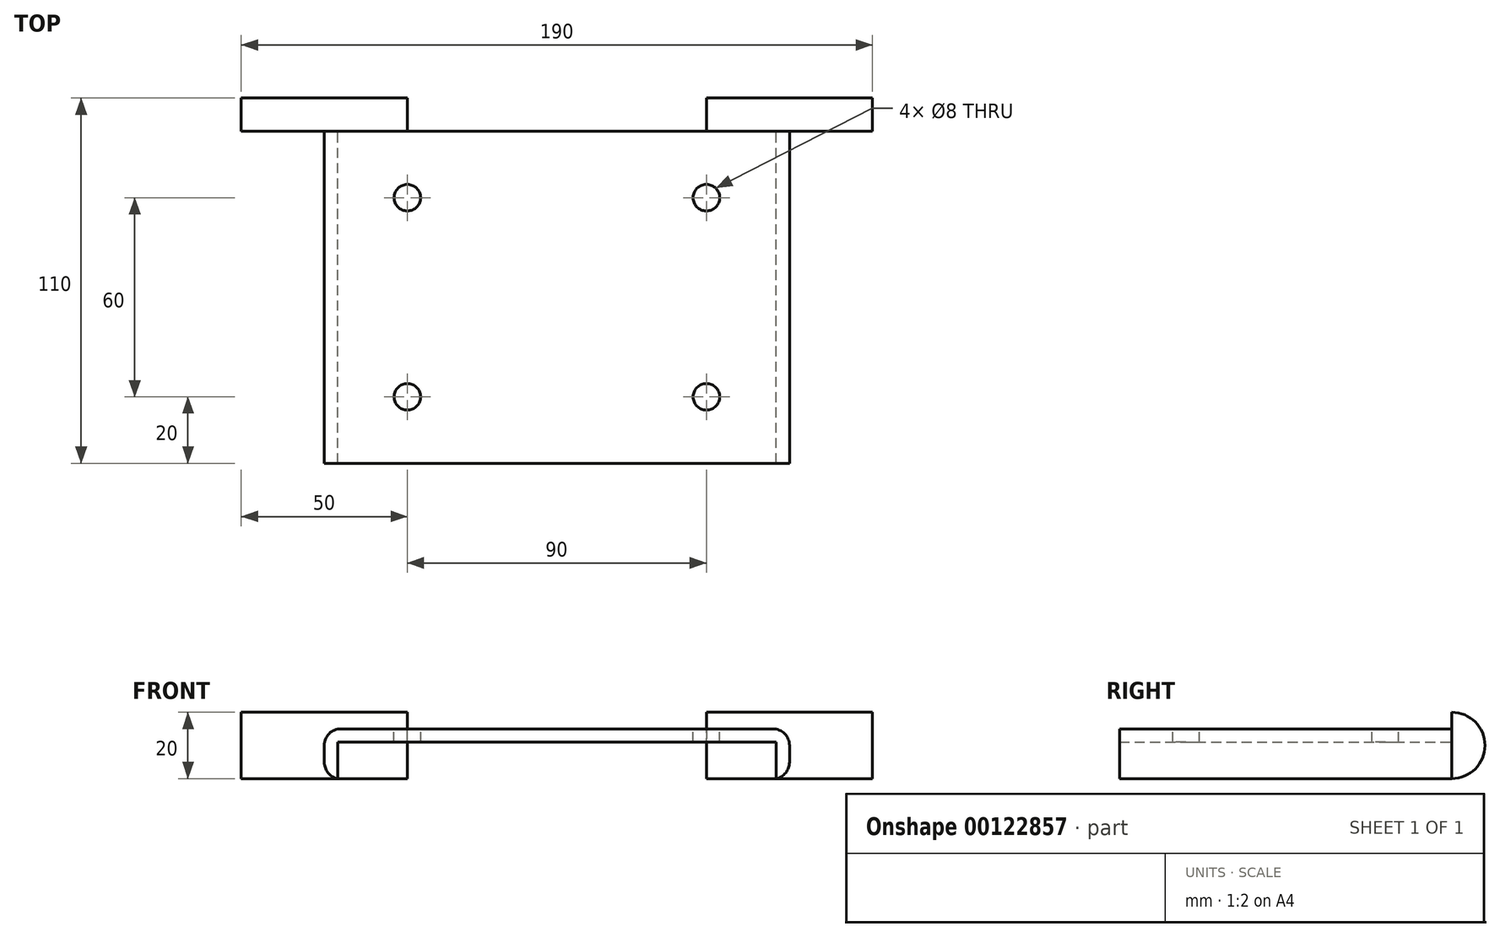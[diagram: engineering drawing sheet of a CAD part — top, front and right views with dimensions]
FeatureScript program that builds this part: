
annotation { "Feature Type Name" : "Feature", "Feature Type Description" : "" }
export const myFeature = defineFeature(function(context is Context, id is Id, definition is map)
    precondition{}
    {
        {
            var Q0;
            Q0=qCreatedBy(makeId("Front.planeOp"),FACE);
            var sketch = newSketch(context, id + "F0", { "sketchPlane" : qUnion([Q0])});
            skLineSegment(sketch, "E0", {"start": v(0, 0) * mm, "end": v(140, 0) * mm});
            skLineSegment(sketch, "E1", {"start": v(140, 0) * mm, "end": v(140, -15) * mm});
            skLineSegment(sketch, "E2", {"start": v(0, 0) * mm, "end": v(0, -15) * mm});
            skLineSegment(sketch, "E3", {"start": v(0, -15) * mm, "end": v(4, -15) * mm});
            skLineSegment(sketch, "E4", {"start": v(4, -15) * mm, "end": v(4, -4) * mm});
            skLineSegment(sketch, "E5", {"start": v(140, -15) * mm, "end": v(136, -15) * mm});
            skLineSegment(sketch, "E6", {"start": v(136, -15) * mm, "end": v(136, -4) * mm});
            skLineSegment(sketch, "E7", {"start": v(136, -4) * mm, "end": v(4, -4) * mm});
            skSolve(sketch);
        }
        {
            var Q0;
            Q0=qSketchRegion(id+"F0",true);
            extrude(context, id + "F1", {"entities" : qUnion([Q0]), "depth" : 100 * mm});
        }
        {
            var Q0;
            Q0=makeQuery(id+"F1.opExtrude","SWEPT_EDGE",EDGE,{"disambiguationData":[OSD([sQuery(id+"F0.wireOp",EDGE,"E0"),sQuery(id+"F0.wireOp",EDGE,"E2")])]});
            var Q1;
            Q1=makeQuery(id+"F1.opExtrude","SWEPT_EDGE",EDGE,{"disambiguationData":[OSD([sQuery(id+"F0.wireOp",EDGE,"E1"),sQuery(id+"F0.wireOp",EDGE,"E5")])]});
            fillet(context, id + "F2", {"entities" : qUnion([Q0, Q1]), "radius" : 5 * mm, "tangentPropagation" : true, "allowEdgeOverflow" : false});
        }
        {
            var Q0;
            Q0=makeQuery(id+"F1.opExtrude","SWEPT_EDGE",EDGE,{"disambiguationData":[OSD([sQuery(id+"F0.wireOp",EDGE,"E2"),sQuery(id+"F0.wireOp",EDGE,"E3")])]});
            var Q1;
            Q1=makeQuery(id+"F1.opExtrude","SWEPT_EDGE",EDGE,{"disambiguationData":[OSD([sQuery(id+"F0.wireOp",EDGE,"E0"),sQuery(id+"F0.wireOp",EDGE,"E1")])]});
            fillet(context, id + "F3", {"entities" : qUnion([Q0, Q1]), "radius" : 5 * mm, "tangentPropagation" : true, "allowEdgeOverflow" : false});
        }
        {
            var Q0;
            Q0=makeQuery(id+"F1.opExtrude","SWEPT_FACE",FACE,{"disambiguationData":[OSD([sQuery(id+"F0.wireOp",EDGE,"E0")])]});
            var sketch = newSketch(context, id + "F4", { "sketchPlane" : qUnion([Q0])});
            skLineSegment(sketch, "E8.0", {"start": v(5, 0) * mm, "end": v(70, 0) * mm, "construction": true});
            skLineSegment(sketch, "E9", {"start": v(70, 0) * mm, "end": v(70, -100) * mm, "construction": true});
            skLineSegment(sketch, "E10", {"start": v(70, -50) * mm, "end": v(70, -20) * mm, "construction": true});
            skLineSegment(sketch, "E11", {"start": v(70, -20) * mm, "end": v(25, -20) * mm, "construction": true});
            skLineSegment(sketch, "E12", {"start": v(70, -20) * mm, "end": v(115, -20) * mm, "construction": true});
            skLineSegment(sketch, "E13", {"start": v(25, -20) * mm, "end": v(25, -80) * mm, "construction": true});
            skLineSegment(sketch, "E14", {"start": v(25, -80) * mm, "end": v(115, -80) * mm, "construction": true});
            skPoint(sketch, "E15", {"position": v(25, -20) * mm});
            skPoint(sketch, "E16", {"position": v(115, -20) * mm});
            skPoint(sketch, "E17", {"position": v(25, -80) * mm});
            skPoint(sketch, "E18", {"position": v(115, -80) * mm});
            skLineSegment(sketch, "E19", {"start": v(70, 10) * mm, "end": v(70, 0) * mm});
            skLineSegment(sketch, "E20", {"start": v(70, 0) * mm, "end": v(70, -1) * mm});
            skLineSegment(sketch, "E21", {"start": v(70, -1) * mm, "end": v(135, -1) * mm});
            skLineSegment(sketch, "E22", {"start": v(135, -1) * mm, "end": v(165, -1) * mm});
            skLineSegment(sketch, "E23", {"start": v(165, -1) * mm, "end": v(165, 10) * mm});
            skLineSegment(sketch, "E24", {"start": v(70, 10) * mm, "end": v(165, 10) * mm});
            skSolve(sketch);
        }
        {
            var Q0;
            Q0=sQuery(id+"F4.wireOp",VERTEX,"E15");
            var Q1;
            Q1=sQuery(id+"F4.wireOp",VERTEX,"E16");
            var Q2;
            Q2=sQuery(id+"F4.wireOp",VERTEX,"E17");
            var Q3;
            Q3=sQuery(id+"F4.wireOp",VERTEX,"E18");
            var Q4;
            Q4=makeQuery(id+"F1.opExtrude","SWEPT_BODY",BODY,{"disambiguationData":[OSD([sQuery(id+"F0.wireOp",EDGE,"E0"),sQuery(id+"F0.wireOp",EDGE,"E1"),sQuery(id+"F0.wireOp",EDGE,"E2"),sQuery(id+"F0.wireOp",EDGE,"E3"),sQuery(id+"F0.wireOp",EDGE,"E4"),sQuery(id+"F0.wireOp",EDGE,"E5"),sQuery(id+"F0.wireOp",EDGE,"E6"),sQuery(id+"F0.wireOp",EDGE,"E7")])]});
            hole(context, id + "F5", {"style" : HoleStyle.SIMPLE, "endStyle" : HoleEndStyle.THROUGH, "holeDiameter" : 8 * mm, "locations" : qUnion([Q0, Q1, Q2, Q3]), "scope" : qUnion([Q4]), "isTappedThrough" : true});
        }
        {
            var Q0;
            Q0=qCreatedBy(makeId("Front.planeOp"),FACE);
            var sketch = newSketch(context, id + "F6", { "sketchPlane" : qUnion([Q0])});
            skLineSegment(sketch, "E25", {"start": v(0, 0) * mm, "end": v(-40, 0) * mm, "construction": true});
            skLineSegment(sketch, "E26", {"start": v(-85, 0) * mm, "end": v(-85, 150) * mm, "construction": true});
            skPoint(sketch, "E26.endSnap0", {"position": v(-85, 0) * mm});
            skLineSegment(sketch, "E27", {"start": v(-130, 100) * mm, "end": v(-130, 0) * mm});
            skLineSegment(sketch, "E28", {"start": v(-40, 0) * mm, "end": v(-40, 100) * mm});
            skArc(sketch, "E29", {"start": v(-40, 100) * mm, "mid": v(-85, 150) * mm, "end": v(-130, 100) * mm});
            skLineSegment(sketch, "E30", {"start": v(-85, 150) * mm, "end": v(-85, 135) * mm, "construction": true});
            skPoint(sketch, "E31.orphan", {"position": v(-145, 100) * mm});
            skPoint(sketch, "E32.end.orphan", {"position": v(-55, 100) * mm});
            skLineSegment(sketch, "E33", {"start": v(-130, 0) * mm, "end": v(-40, 0) * mm, "construction": true});
            skSolve(sketch);
        }
        {
            var Q0;
            Q0=qCreatedBy(makeId("Top.planeOp"),FACE);
            var sketch = newSketch(context, id + "F7", { "sketchPlane" : qUnion([Q0])});
            skLineSegment(sketch, "E34", {"start": v(0, 0) * mm, "end": v(-40, 0) * mm, "construction": true});
            skCircle(sketch, "E35", {"center": v(-40, 0) * mm, "radius": 7.5 * mm});
            skSolve(sketch);
        }
        {
            var Q0;
            Q0=makeQuery(id+"F7.imprint","IMPRINT",FACE,{"disambiguationData":[TD([[makeQuery(id+"F7.imprint","IMPRINT",EDGE,{"derivedFrom":sQuery(id+"F7.wireOp",EDGE,"E35")}),1.0]])]});
            var Q1;
            Q1=sQuery(id+"F7.wireOp",EDGE,"E35");
            var Q2;
            Q2=sQuery(id+"F6.wireOp",EDGE,"E28");
            var Q3;
            Q3=sQuery(id+"F6.wireOp",EDGE,"E29");
            var Q4;
            Q4=sQuery(id+"F6.wireOp",EDGE,"E27");
            sweep(context, id + "F8", {"profiles" : qUnion([Q0]), "surfaceProfiles" : qUnion([Q1]), "path" : qUnion([Q2, Q3, Q4])});
        }
        {
            var Q0;
            Q0=qCreatedBy(makeId("Right.planeOp"),FACE);
            var sketch = newSketch(context, id + "F9", { "sketchPlane" : qUnion([Q0])});
            skLineSegment(sketch, "E36.0", {"start": v(0, 0) * mm, "end": v(0, -5) * mm});
            skArc(sketch, "E37", {"start": v(0, -15) * mm, "mid": v(10, -5) * mm, "end": v(0, 5) * mm});
            skLineSegment(sketch, "E38", {"start": v(0, 0) * mm, "end": v(0, 5) * mm});
            skLineSegment(sketch, "E39", {"start": v(0, -5) * mm, "end": v(0, -15) * mm});
            skSolve(sketch);
        }
        {
            var Q0;
            Q0=qSketchRegion(id+"F9",true);
            extrude(context, id + "F10", {"entities" : qUnion([Q0]), "operationType" : NewBodyOperationType.ADD, "endBound" : BoundingType.SYMMETRIC, "depth" : 50 * mm});
        }
        {
            var Q0;
            Q0=makeQuery(id+"F8.opSweep","SWEPT_BODY",BODY,{"disambiguationData":[OSD([sQuery(id+"F6.wireOp",EDGE,"E27"),sQuery(id+"F7.wireOp",EDGE,"E35")])]});
            deleteBodies(context, id + "F11", {"entities" : qUnion([Q0])});
        }
        {
            var Q0;
            Q0=qCreatedBy(makeId("Right.planeOp"),FACE);
            cPlane(context, id + "F12", {"entities" : qUnion([Q0]), "cplaneType" : CPlaneType.OFFSET, "offset" : 140 * mm, "width" : 150 * mm, "height" : 150 * mm});
        }
        {
            var Q0;
            Q0=qCreatedBy(id+"F12.planeOp",FACE);
            var sketch = newSketch(context, id + "F13", { "sketchPlane" : qUnion([Q0])});
            skArc(sketch, "E40.0", {"start": v(0, -15) * mm, "mid": v(10, -5) * mm, "end": v(0, 5) * mm});
            skLineSegment(sketch, "E41.0", {"start": v(0, -5) * mm, "end": v(0, -10.1) * mm});
            skLineSegment(sketch, "E42.0", {"start": v(0, 0) * mm, "end": v(0, -5) * mm});
            skLineSegment(sketch, "E43.0", {"start": v(0, -10.1) * mm, "end": v(0, -15) * mm});
            skLineSegment(sketch, "E44", {"start": v(0, 0) * mm, "end": v(0, 5) * mm});
            skSolve(sketch);
        }
        {
            var Q0;
            Q0 = qSketchRegion(id + "F13", true);
            extrude(context, id + "F14", {"entities" : qUnion([Q0]), "operationType" : NewBodyOperationType.ADD, "endBound" : BoundingType.SYMMETRIC, "depth" : 50 * mm});
        }
    });
